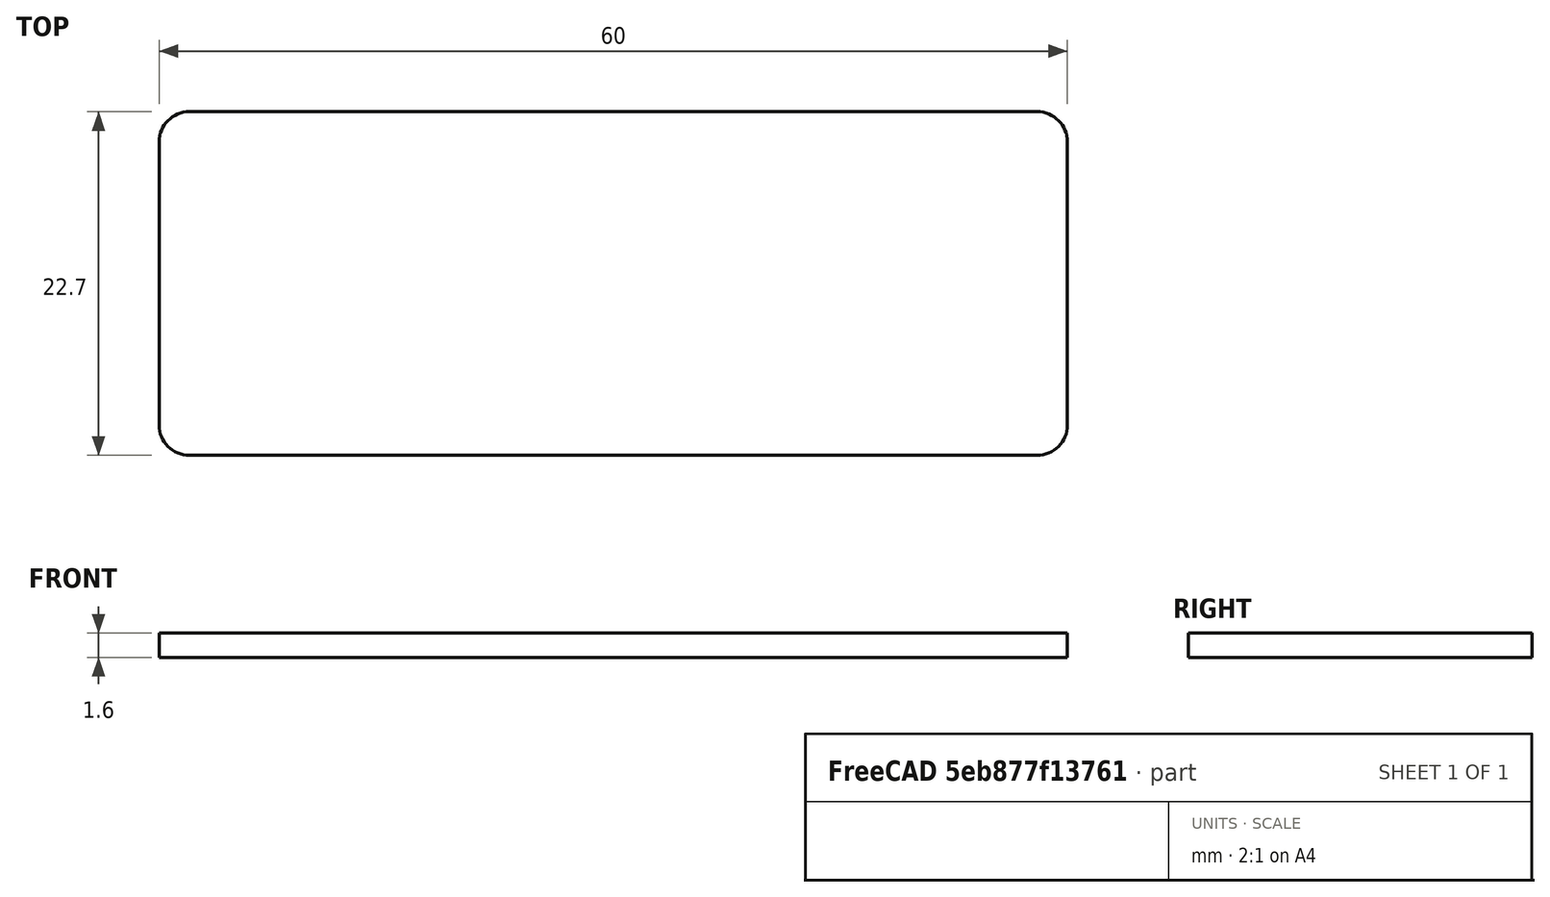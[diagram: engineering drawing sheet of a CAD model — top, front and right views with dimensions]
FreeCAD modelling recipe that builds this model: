
FCSTD DOCUMENT  (FreeCAD 1.0R39109 (Git))
Label: coverplate
License: All rights reserved
LicenseURL: https://en.wikipedia.org/wiki/All_rights_reserved
objects: Spreadsheet::Sheet×1, Sketcher::SketchObject×1, PartDesign::Pad×1, PartDesign::Body×1
note: 6 computed .brp shape members not serialized (recipe doc carries the construction recipe); baked Part::Feature solids carry a one-line shape summary decoded from their .brp

FEATURE [Spreadsheet::Sheet] Spreadsheet
  cells = A1='Plate thickness; B1(PlateThick)=1.6; A2='Plate width; B2(PlateWidth)=60; A3='Plate height; B3(PlateHeight)=22.7; A4='Plate fillet; B4(PlateFillet)=2
FEATURE [Sketcher::SketchObject] Sketch
  ArcFitTolerance = 1e-06
  AttachmentSupport = -> [XY_Plane]
  FullyConstrained = true
  MakeInternals = false
  MapMode = 5
  expr: Constraints[23] = Spreadsheet.PlateFillet
  expr: Constraints[5] = Spreadsheet.PlateWidth
  expr: Constraints[6] = Spreadsheet.PlateHeight
  sketch-geometry (12):
    g0: LineSegment StartX=-30 StartY=9.35 StartZ=0 EndX=-30 EndY=-9.35 EndZ=0
    g1: LineSegment StartX=-28 StartY=-11.35 StartZ=0 EndX=28 EndY=-11.35 EndZ=0
    g2: LineSegment StartX=30 StartY=-9.35 StartZ=0 EndX=30 EndY=9.35 EndZ=0
    g3: LineSegment StartX=28 StartY=11.35 StartZ=0 EndX=-28 EndY=11.35 EndZ=0
    g4: ArcOfCircle CenterX=-28 CenterY=-9.35 CenterZ=0 NormalX=0 NormalY=0 NormalZ=1 AngleXU=0 Radius=2 StartAngle=3.14159 EndAngle=4.71239
    g5: GeomPoint [constr] X=-30 Y=-11.35 Z=0
    g6: ArcOfCircle CenterX=-28 CenterY=9.35 CenterZ=0 NormalX=0 NormalY=0 NormalZ=1 AngleXU=0 Radius=2 StartAngle=1.5708 EndAngle=3.14159
    g7: GeomPoint [constr] X=-30 Y=11.35 Z=0
    g8: ArcOfCircle CenterX=28 CenterY=9.35 CenterZ=0 NormalX=0 NormalY=0 NormalZ=1 AngleXU=0 Radius=2 StartAngle=3.1e-15 EndAngle=1.5708
    g9: GeomPoint [constr] X=30 Y=11.35 Z=0
    g10: ArcOfCircle CenterX=28 CenterY=-9.35 CenterZ=0 NormalX=0 NormalY=0 NormalZ=1 AngleXU=0 Radius=2 StartAngle=4.71239 EndAngle=6.28319
    g11: GeomPoint [constr] X=30 Y=-11.35 Z=0
  constraints (27):
    c: Vertical(g0)
    c: Vertical(g2)
    c: Horizontal(g1)
    c: Horizontal(g3)
    c: Symmetric(g9,g5,g-1)
    c: DistanceX(g5,g11) = 60
    c: DistanceY(g11,g9) = 22.7
    c: PointOnObject(g5,g1)
    c: PointOnObject(g5,g0)
    c: Tangent(g1,g4) = -1.5708
    c: Tangent(g0,g4) = -1.5708
    c: PointOnObject(g7,g3)
    c: PointOnObject(g7,g0)
    c: Tangent(g3,g6) = -1.5708
    c: Tangent(g0,g6) = -1.5708
    c: PointOnObject(g9,g2)
    c: PointOnObject(g9,g3)
    c: Tangent(g2,g8) = -1.5708
    c: Tangent(g3,g8) = -1.5708
    c: PointOnObject(g11,g2)
    c: PointOnObject(g11,g1)
    c: Tangent(g2,g10) = -1.5708
    c: Tangent(g1,g10) = -1.5708
    c: DistanceY(g1,g4) = 2
    c: Equal(g4,g6)
    c: Equal(g4,g8)
    c: Equal(g4,g10)
FEATURE [PartDesign::Pad] Pad
  Direction = (0,0,1)
  Length = 1.6
  Length2 = 10
  Profile = -> Sketch
  ReferenceAxis = -> Sketch [N_Axis]
  Refine = true
  Suppressed = false
  Type = 0
  expr: Length = Spreadsheet.PlateThick
FEATURE [PartDesign::Body] Body
  AllowCompound = false
  Group = -> [Sketch,Pad]
  Origin = -> Origin
  Tip = -> Pad
